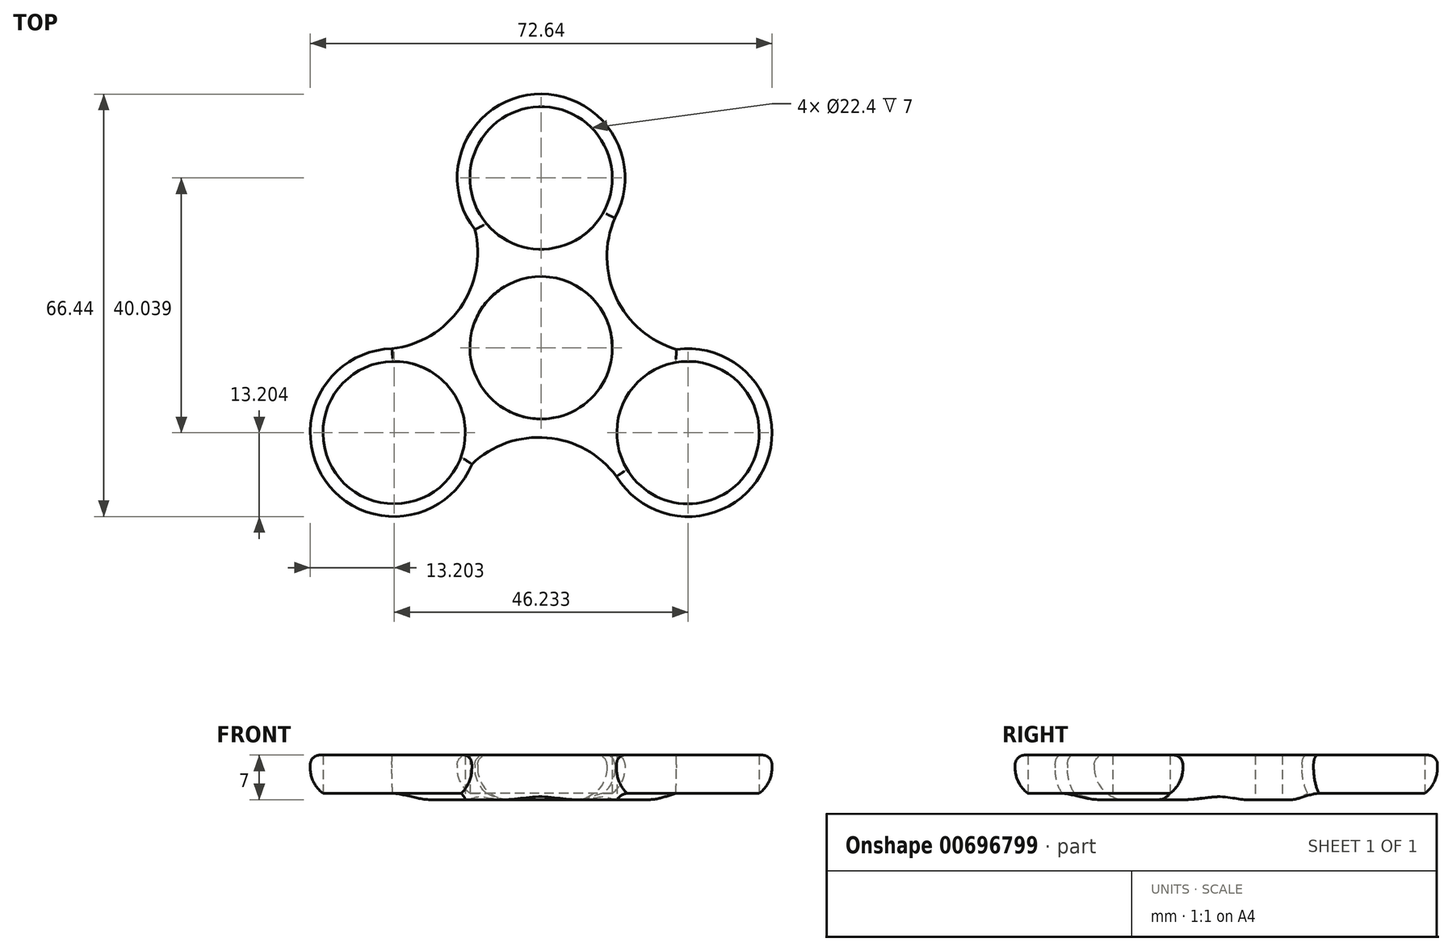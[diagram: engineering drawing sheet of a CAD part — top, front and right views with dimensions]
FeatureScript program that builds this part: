
annotation { "Feature Type Name" : "Feature", "Feature Type Description" : "" }
export const myFeature = defineFeature(function(context is Context, id is Id, definition is map)
    precondition{}
    {
        {
            var Q0;
            Q0=qCreatedBy(makeId("Top.planeOp"),FACE);
            var sketch = newSketch(context, id + "F0", { "sketchPlane" : qUnion([Q0])});
            skCircle(sketch, "E0", {"center": v(0, 0) * mm, "radius": 11.2 * mm});
            skCircle(sketch, "E1", {"center": v(0, 26.7) * mm, "radius": 11.2 * mm});
            skArc(sketch, "E2", {"start": v(11.6, 20.4) * mm, "mid": v(-1.08, 39.85) * mm, "end": v(-10.42, 18.59) * mm});
            skCircle(sketch, "E3.1.0", {"center": v(-23.12, -13.35) * mm, "radius": 11.2 * mm});
            skArc(sketch, "E3.1.1", {"start": v(-23.47, -0.15) * mm, "mid": v(-33.97, -20.86) * mm, "end": v(-10.89, -18.31) * mm});
            skCircle(sketch, "E3.2.0", {"center": v(23.12, -13.35) * mm, "radius": 11.2 * mm});
            skArc(sketch, "E3.2.1", {"start": v(11.86, -20.25) * mm, "mid": v(35.05, -18.99) * mm, "end": v(21.3, -0.27) * mm});
            skArc(sketch, "E4", {"start": v(11.6, 20.4) * mm, "mid": v(11.8, 7.88) * mm, "end": v(21.3, -0.27) * mm});
            skArc(sketch, "E5.1.0", {"start": v(-23.47, -0.15) * mm, "mid": v(-12.72, 6.28) * mm, "end": v(-10.42, 18.59) * mm});
            skArc(sketch, "E5.2.0", {"start": v(11.86, -20.25) * mm, "mid": v(0.92, -14.15) * mm, "end": v(-10.89, -18.31) * mm});
            skSolve(sketch);
        }
        {
            var Q0;
            Q0=makeQuery(id+"F0.imprint","IMPRINT",FACE,{"disambiguationData":[TD([[makeQuery(id+"F0.imprint","IMPRINT",EDGE,{"derivedFrom":sQuery(id+"F0.wireOp",EDGE,"E0")}),-1.0]])]});
            extrude(context, id + "F1", {"entities" : qUnion([Q0]), "depth" : 7 * mm, "offsetDistance" : 25 * mm});
        }
        {
            var Q0;
            Q0=makeQuery(id+"F1.opExtrude","CAP_EDGE",EDGE,{"disambiguationData":[OSD([sQuery(id+"F0.wireOp",EDGE,"E5.1.0")])],"isStart":false});
            var Q1;
            Q1=makeQuery(id+"F1.opExtrude","CAP_EDGE",EDGE,{"disambiguationData":[OSD([sQuery(id+"F0.wireOp",EDGE,"E3.1.1")])],"isStart":false});
            var Q2;
            Q2=makeQuery(id+"F1.opExtrude","CAP_EDGE",EDGE,{"disambiguationData":[OSD([sQuery(id+"F0.wireOp",EDGE,"E5.2.0")])],"isStart":false});
            var Q3;
            Q3=makeQuery(id+"F1.opExtrude","CAP_EDGE",EDGE,{"disambiguationData":[OSD([sQuery(id+"F0.wireOp",EDGE,"E3.2.1")])],"isStart":false});
            var Q4;
            Q4=makeQuery(id+"F1.opExtrude","CAP_EDGE",EDGE,{"disambiguationData":[OSD([sQuery(id+"F0.wireOp",EDGE,"E4")])],"isStart":false});
            var Q5;
            Q5=makeQuery(id+"F1.opExtrude","CAP_EDGE",EDGE,{"disambiguationData":[OSD([sQuery(id+"F0.wireOp",EDGE,"E2")])],"isStart":false});
            fillet(context, id + "F2", {"entities" : qUnion([Q0, Q1, Q2, Q3, Q4, Q5]), "radius" : 1.5 * mm, "tangentPropagation" : true, "allowEdgeOverflow" : false});
        }
        {
            var Q0;
            Q0=makeQuery(id+"F1.opExtrude","CAP_EDGE",EDGE,{"disambiguationData":[OSD([sQuery(id+"F0.wireOp",EDGE,"E4")])],"isStart":true});
            var Q1;
            Q1=makeQuery(id+"F1.opExtrude","CAP_EDGE",EDGE,{"disambiguationData":[OSD([sQuery(id+"F0.wireOp",EDGE,"E3.2.1")])],"isStart":true});
            var Q2;
            Q2=makeQuery(id+"F1.opExtrude","CAP_EDGE",EDGE,{"disambiguationData":[OSD([sQuery(id+"F0.wireOp",EDGE,"E5.2.0")])],"isStart":true});
            var Q3;
            Q3=makeQuery(id+"F1.opExtrude","CAP_EDGE",EDGE,{"disambiguationData":[OSD([sQuery(id+"F0.wireOp",EDGE,"E3.1.1")])],"isStart":true});
            var Q4;
            Q4=makeQuery(id+"F1.opExtrude","CAP_EDGE",EDGE,{"disambiguationData":[OSD([sQuery(id+"F0.wireOp",EDGE,"E5.1.0")])],"isStart":true});
            var Q5;
            Q5=makeQuery(id+"F1.opExtrude","CAP_EDGE",EDGE,{"disambiguationData":[OSD([sQuery(id+"F0.wireOp",EDGE,"E2")])],"isStart":true});
            fillet(context, id + "F3", {"entities" : qUnion([Q0, Q1, Q2, Q3, Q4, Q5]), "radius" : 5 * mm, "tangentPropagation" : true, "allowEdgeOverflow" : false});
        }
    });
